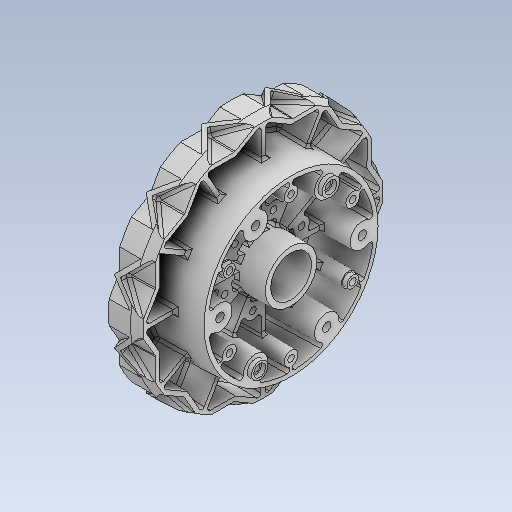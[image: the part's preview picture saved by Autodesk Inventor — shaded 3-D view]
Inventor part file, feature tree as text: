
AUTODESK INVENTOR PART (.ipt)
format: ipt  version: 2020.2 (Build 242310000, 310)  size: 2,922,496 bytes
history: native  units: in
note: dims shown in document units (in); Inventor stores cm internally (conversion verified against a paired STEP export)
features: fillet x1
ambient origin geometry x8: Origin, YZ Plane, XZ Plane, XY Plane, X Axis, Y Axis, Z Axis, Center Point
bodies: Solid1 (feature_tree)
feature tree (1):
  fillet  "Fillet141"  [1 undecoded]
note: 1 required parameter value undecoded (feature->parameter linkage not recoverable at this tier; creation-order binding heuristic only, values carry confidence <= 0.55)
